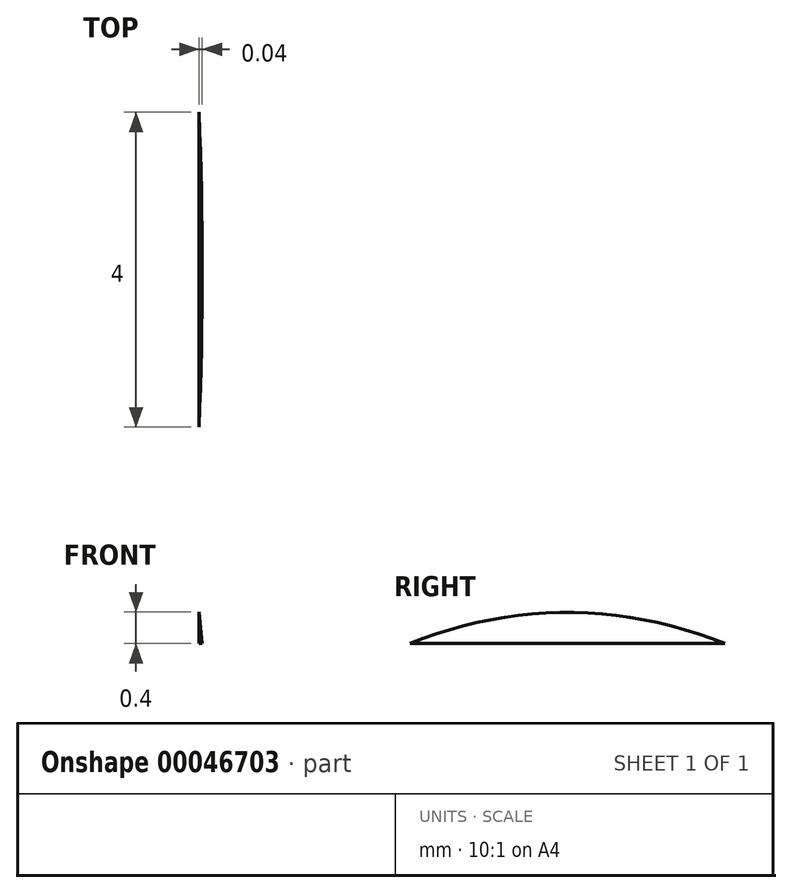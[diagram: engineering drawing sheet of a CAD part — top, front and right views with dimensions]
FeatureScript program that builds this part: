
annotation { "Feature Type Name" : "Feature", "Feature Type Description" : "" }
export const myFeature = defineFeature(function(context is Context, id is Id, definition is map)
    precondition{}
    {
        {
            var Q0;
            Q0=qCreatedBy(makeId("Top.planeOp"),FACE);
            var sketch = newSketch(context, id + "F0", { "sketchPlane" : qUnion([Q0])});
            skCircle(sketch, "E0", {"center": v(0, 0) * mm, "radius": 50 * mm});
            skLineSegment(sketch, "E1.rect.bottom", {"start": v(34.96, 25) * mm, "end": v(27.46, 25) * mm, "construction": true});
            skLineSegment(sketch, "E1.rect.top", {"start": v(34.96, -25) * mm, "end": v(27.46, -25) * mm, "construction": true});
            skLineSegment(sketch, "E1.rect.left", {"start": v(34.96, 25) * mm, "end": v(34.96, 17.5) * mm, "construction": true});
            skLineSegment(sketch, "E1.rect.right", {"start": v(-11.94, 25) * mm, "end": v(-11.94, 17.5) * mm, "construction": true});
            skPoint(sketch, "E1.rect.middle", {"position": v(11.51, 0) * mm});
            skLineSegment(sketch, "E2.bottom", {"start": v(34.96, -2) * mm, "end": v(49.96, -2) * mm});
            skLineSegment(sketch, "E2.top", {"start": v(34.96, 2) * mm, "end": v(49.96, 2) * mm});
            skLineSegment(sketch, "E2.left", {"start": v(34.96, -2) * mm, "end": v(34.96, 2) * mm});
            skLineSegment(sketch, "E2.right", {"start": v(49.96, -2) * mm, "end": v(49.96, 2) * mm});
            skLineSegment(sketch, "E3", {"start": v(0, 0) * mm, "end": v(0, 50) * mm, "construction": true});
            skLineSegment(sketch, "E4", {"start": v(0, 0) * mm, "end": v(0, -50) * mm, "construction": true});
            skCircle(sketch, "E5", {"center": v(0, 33.5) * mm, "radius": 1.5 * mm});
            skLineSegment(sketch, "E6", {"start": v(-11.94, 0) * mm, "end": v(-41.83, 0) * mm, "construction": true});
            skLineSegment(sketch, "E7", {"start": v(-11.94, 2) * mm, "end": v(-31.94, 2) * mm});
            skLineSegment(sketch, "E8", {"start": v(-11.94, -2) * mm, "end": v(-31.94, -2) * mm});
            skArc(sketch, "E9", {"start": v(0, 32) * mm, "mid": v(-32, 0) * mm, "end": v(0, -32) * mm});
            skArc(sketch, "E10", {"start": v(0, 35) * mm, "mid": v(-35, 0) * mm, "end": v(0, -35) * mm});
            skLineSegment(sketch, "E11", {"start": v(0, 0) * mm, "end": v(-33.8, 9.06) * mm, "construction": true});
            skLineSegment(sketch, "E12", {"start": v(0, 0) * mm, "end": v(-33.8, -9.06) * mm, "construction": true});
            skCircle(sketch, "E13", {"center": v(-32.36, 8.67) * mm, "radius": 1.5 * mm});
            skCircle(sketch, "E14", {"center": v(0, -33.5) * mm, "radius": 1.5 * mm});
            skCircle(sketch, "E15", {"center": v(-32.36, -8.67) * mm, "radius": 1.5 * mm});
            skLineSegment(sketch, "E16", {"start": v(-4.44, 25) * mm, "end": v(-11.94, 25) * mm, "construction": true});
            skArc(sketch, "E17", {"start": v(-11.94, 17.5) * mm, "mid": v(0.87, 12.2) * mm, "end": v(-4.44, 25) * mm, "construction": true});
            skArc(sketch, "E18", {"start": v(-4.44, 25) * mm, "mid": v(-9.74, 22.8) * mm, "end": v(-11.94, 17.5) * mm});
            skLineSegment(sketch, "E19", {"start": v(-11.94, 17.5) * mm, "end": v(-11.94, -17.5) * mm});
            skLineSegment(sketch, "E20", {"start": v(-11.94, -17.5) * mm, "end": v(-11.94, -25) * mm, "construction": true});
            skArc(sketch, "E21", {"start": v(-4.44, -25) * mm, "mid": v(0.87, -12.2) * mm, "end": v(-11.94, -17.5) * mm, "construction": true});
            skArc(sketch, "E22", {"start": v(-11.94, -17.5) * mm, "mid": v(-9.74, -22.8) * mm, "end": v(-4.44, -25) * mm});
            skLineSegment(sketch, "E23", {"start": v(-4.44, -25) * mm, "end": v(-11.94, -25) * mm, "construction": true});
            skArc(sketch, "E24", {"start": v(27.46, -25) * mm, "mid": v(32.76, -22.8) * mm, "end": v(34.96, -17.5) * mm});
            skArc(sketch, "E25", {"start": v(34.96, -17.5) * mm, "mid": v(22.16, -12.2) * mm, "end": v(27.46, -25) * mm, "construction": true});
            skLineSegment(sketch, "E26", {"start": v(34.96, -17.5) * mm, "end": v(34.96, -25) * mm, "construction": true});
            skLineSegment(sketch, "E27", {"start": v(27.46, -25) * mm, "end": v(-4.44, -25) * mm});
            skLineSegment(sketch, "E28", {"start": v(34.96, 17.5) * mm, "end": v(34.96, -17.5) * mm});
            skLineSegment(sketch, "E29", {"start": v(27.46, 25) * mm, "end": v(-4.44, 25) * mm});
            skArc(sketch, "E30", {"start": v(27.46, 25) * mm, "mid": v(22.16, 12.2) * mm, "end": v(34.96, 17.5) * mm, "construction": true});
            skArc(sketch, "E31", {"start": v(34.96, 17.5) * mm, "mid": v(32.76, 22.8) * mm, "end": v(27.46, 25) * mm});
            skSolve(sketch);
        }
        {
            var Q0;
            Q0=qCreatedBy(makeId("Front.planeOp"),FACE);
            var sketch = newSketch(context, id + "F1", { "sketchPlane" : qUnion([Q0])});
            skLineSegment(sketch, "E32", {"start": v(0, 0) * mm, "end": v(0, 25) * mm});
            skLineSegment(sketch, "E33", {"start": v(0, 25) * mm, "end": v(-47.5, 25) * mm});
            skLineSegment(sketch, "E34", {"start": v(-47.5, 25) * mm, "end": v(-50, 0) * mm});
            skLineSegment(sketch, "E35", {"start": v(-50, 0) * mm, "end": v(0, 0) * mm});
            skSolve(sketch);
        }
        {
            var Q0;
            Q0 = qSketchRegion(id + "F1", true);
            var Q1;
            Q1=sQuery(id+"F1.wireOp",EDGE,"E32");
            revolve(context, id + "F2", {"entities" : qUnion([Q0]), "axis" : qUnion([Q1]), "revolveType" : RevolveType.FULL});
        }
        {
            var Q0;
            {var subQ2=sQuery(id+"F0.wireOp",EDGE,"E2.bottom");Q0=makeQuery(id+"F0.imprint","IMPRINT",FACE,{"disambiguationData":[TD([[makeQuery(id+"F0.imprint","IMPRINT",EDGE,{"derivedFrom":subQ2}),1.0]])]});}
            var Q1;
            {var subQ2=sQuery(id+"F0.wireOp",EDGE,"E7");Q1=makeQuery(id+"F0.imprint","IMPRINT",FACE,{"disambiguationData":[TD([[makeQuery(id+"F0.imprint","IMPRINT",EDGE,{"derivedFrom":subQ2}),1.0]])]});}
            extrude(context, id + "F3", {"entities" : qUnion([Q0, Q1]), "operationType" : NewBodyOperationType.REMOVE, "depth" : 3 * mm});
        }
        {
            var Q0;
            {var subQ1=sQuery(id+"F0.wireOp",EDGE,"E18");Q0=makeQuery(id+"F0.imprint","IMPRINT",FACE,{"disambiguationData":[TD([[makeQuery(id+"F0.imprint","IMPRINT",EDGE,{"derivedFrom":subQ1}),1.0]])]});}
            extrude(context, id + "F4", {"entities" : qUnion([Q0]), "operationType" : NewBodyOperationType.REMOVE, "depth" : 14 * mm});
        }
        {
            var Q0;
            {var subQ3=sQuery(id+"F0.wireOp",EDGE,"E9");var subQ5=sQuery(id+"F0.wireOp",EDGE,"E14");var subQ7=makeQuery(id+"F0.imprint","INTERSECT",VERTEX,{"derivedFrom":[subQ3,subQ5]});Q0=makeQuery(id+"F0.imprint","IMPRINT",FACE,{"disambiguationData":[TD([[makeQuery(id+"F0.imprint","IMPRINT",EDGE,{"disambiguationData":[TD([[subQ7,1.0]])],"derivedFrom":subQ3}),-1.0]])]});}
            var Q1;
            {var subQ3=sQuery(id+"F0.wireOp",EDGE,"E9");var subQ5=sQuery(id+"F0.wireOp",EDGE,"E5");var subQ7=makeQuery(id+"F0.imprint","INTERSECT",VERTEX,{"derivedFrom":[subQ5,subQ3]});Q1=makeQuery(id+"F0.imprint","IMPRINT",FACE,{"disambiguationData":[TD([[makeQuery(id+"F0.imprint","IMPRINT",EDGE,{"disambiguationData":[TD([[subQ7,1.0]])],"derivedFrom":subQ5}),-1.0]])]});}
            var Q2;
            {var subQ3=sQuery(id+"F0.wireOp",EDGE,"E9");var subQ8=makeQuery(id+"F0.imprint","INTERSECT",VERTEX,{"derivedFrom":[sQuery(id+"F0.wireOp",EDGE,"E7"),subQ3]});Q2=makeQuery(id+"F0.imprint","IMPRINT",FACE,{"disambiguationData":[TD([[makeQuery(id+"F0.imprint","IMPRINT",EDGE,{"disambiguationData":[TD([[subQ8,1.0]])],"derivedFrom":subQ3}),-1.0]])]});}
            var Q3;
            {var subQ0=sQuery(id+"F0.wireOp",EDGE,"E15");var subQ2=makeQuery(id+"F0.imprint","INTERSECT",VERTEX,{"derivedFrom":[sQuery(id+"F0.wireOp",EDGE,"E9"),subQ0]});Q3=makeQuery(id+"F0.imprint","IMPRINT",FACE,{"disambiguationData":[TD([[makeQuery(id+"F0.imprint","IMPRINT",EDGE,{"disambiguationData":[TD([[subQ2,-1.0]])],"derivedFrom":subQ0}),1.0]])]});}
            var Q4;
            {var subQ0=sQuery(id+"F0.wireOp",EDGE,"E13");var subQ2=makeQuery(id+"F0.imprint","INTERSECT",VERTEX,{"derivedFrom":[sQuery(id+"F0.wireOp",EDGE,"E9"),subQ0]});Q4=makeQuery(id+"F0.imprint","IMPRINT",FACE,{"disambiguationData":[TD([[makeQuery(id+"F0.imprint","IMPRINT",EDGE,{"disambiguationData":[TD([[subQ2,1.0]])],"derivedFrom":subQ0}),1.0]])]});}
            extrude(context, id + "F5", {"entities" : qUnion([Q0, Q1, Q2, Q3, Q4]), "operationType" : NewBodyOperationType.REMOVE, "depth" : 2 * mm});
        }
        {
            var Q0;
            {var subQ0=sQuery(id+"F0.wireOp",EDGE,"E15");var subQ2=makeQuery(id+"F0.imprint","INTERSECT",VERTEX,{"derivedFrom":[sQuery(id+"F0.wireOp",EDGE,"E9"),subQ0]});Q0=makeQuery(id+"F0.imprint","IMPRINT",FACE,{"disambiguationData":[TD([[makeQuery(id+"F0.imprint","IMPRINT",EDGE,{"disambiguationData":[TD([[subQ2,-1.0]])],"derivedFrom":subQ0}),1.0]])]});}
            var Q1;
            {var subQ0=sQuery(id+"F0.wireOp",EDGE,"E13");var subQ2=makeQuery(id+"F0.imprint","INTERSECT",VERTEX,{"derivedFrom":[sQuery(id+"F0.wireOp",EDGE,"E9"),subQ0]});Q1=makeQuery(id+"F0.imprint","IMPRINT",FACE,{"disambiguationData":[TD([[makeQuery(id+"F0.imprint","IMPRINT",EDGE,{"disambiguationData":[TD([[subQ2,1.0]])],"derivedFrom":subQ0}),1.0]])]});}
            extrude(context, id + "F6", {"entities" : qUnion([Q0, Q1]), "operationType" : NewBodyOperationType.REMOVE, "depth" : 10 * mm});
        }
        {
            var Q0;
            Q0=makeQuery(id+"F2.opRevolve","SWEPT_EDGE",EDGE,{"disambiguationData":[OSD([sQuery(id+"F1.wireOp",EDGE,"E33"),sQuery(id+"F1.wireOp",EDGE,"E34")])]});
            chamfer(context, id + "F7", {"entities" : qUnion([Q0]), "chamferType" : ChamferType.OFFSET_ANGLE, "width" : 2 * mm, "oppositeDirection" : false, "angle" : 45 * degree});
        }
        {
            var Q0;
            {var subQ0=sQuery(id+"F0.wireOp",EDGE,"E5");var subQ2=makeQuery(id+"F0.imprint","INTERSECT",VERTEX,{"derivedFrom":[subQ0,sQuery(id+"F0.wireOp",EDGE,"E9")]});Q0=makeQuery(id+"F0.imprint","IMPRINT",FACE,{"disambiguationData":[TD([[makeQuery(id+"F0.imprint","IMPRINT",EDGE,{"disambiguationData":[TD([[subQ2,1.0]])],"derivedFrom":subQ0}),1.0]])]});}
            var Q1;
            {var subQ0=sQuery(id+"F0.wireOp",EDGE,"E14");var subQ2=makeQuery(id+"F0.imprint","INTERSECT",VERTEX,{"derivedFrom":[sQuery(id+"F0.wireOp",EDGE,"E9"),subQ0]});Q1=makeQuery(id+"F0.imprint","IMPRINT",FACE,{"disambiguationData":[TD([[makeQuery(id+"F0.imprint","IMPRINT",EDGE,{"disambiguationData":[TD([[subQ2,-1.0]])],"derivedFrom":subQ0}),1.0]])]});}
            extrude(context, id + "F8", {"entities" : qUnion([Q0, Q1]), "operationType" : NewBodyOperationType.REMOVE, "endBound" : BoundingType.THROUGH_ALL, "depth" : 25 * mm});
        }
        {
            var Q0;
            {var subQ0=sQuery(id+"F1.wireOp",EDGE,"E34");var subQ1=sQuery(id+"F1.wireOp",EDGE,"E35");Q0=makeQuery(id+"F3.boolean.opBoolean","SPLIT",EDGE,{"disambiguationData":[TD([makeQuery(id+"F3.opExtrude","SWEPT_FACE",FACE,{"disambiguationData":[OSD([sQuery(id+"F0.wireOp",EDGE,"E2.bottom")])]})])],"derivedFrom":makeQuery(id+"F2.opRevolve","SWEPT_EDGE",EDGE,{"disambiguationData":[OSD([subQ0,subQ1])]})});}
            chamfer(context, id + "F9", {"entities" : qUnion([Q0]), "width" : 2 * mm, "tangentPropagation" : true});
        }
    });
